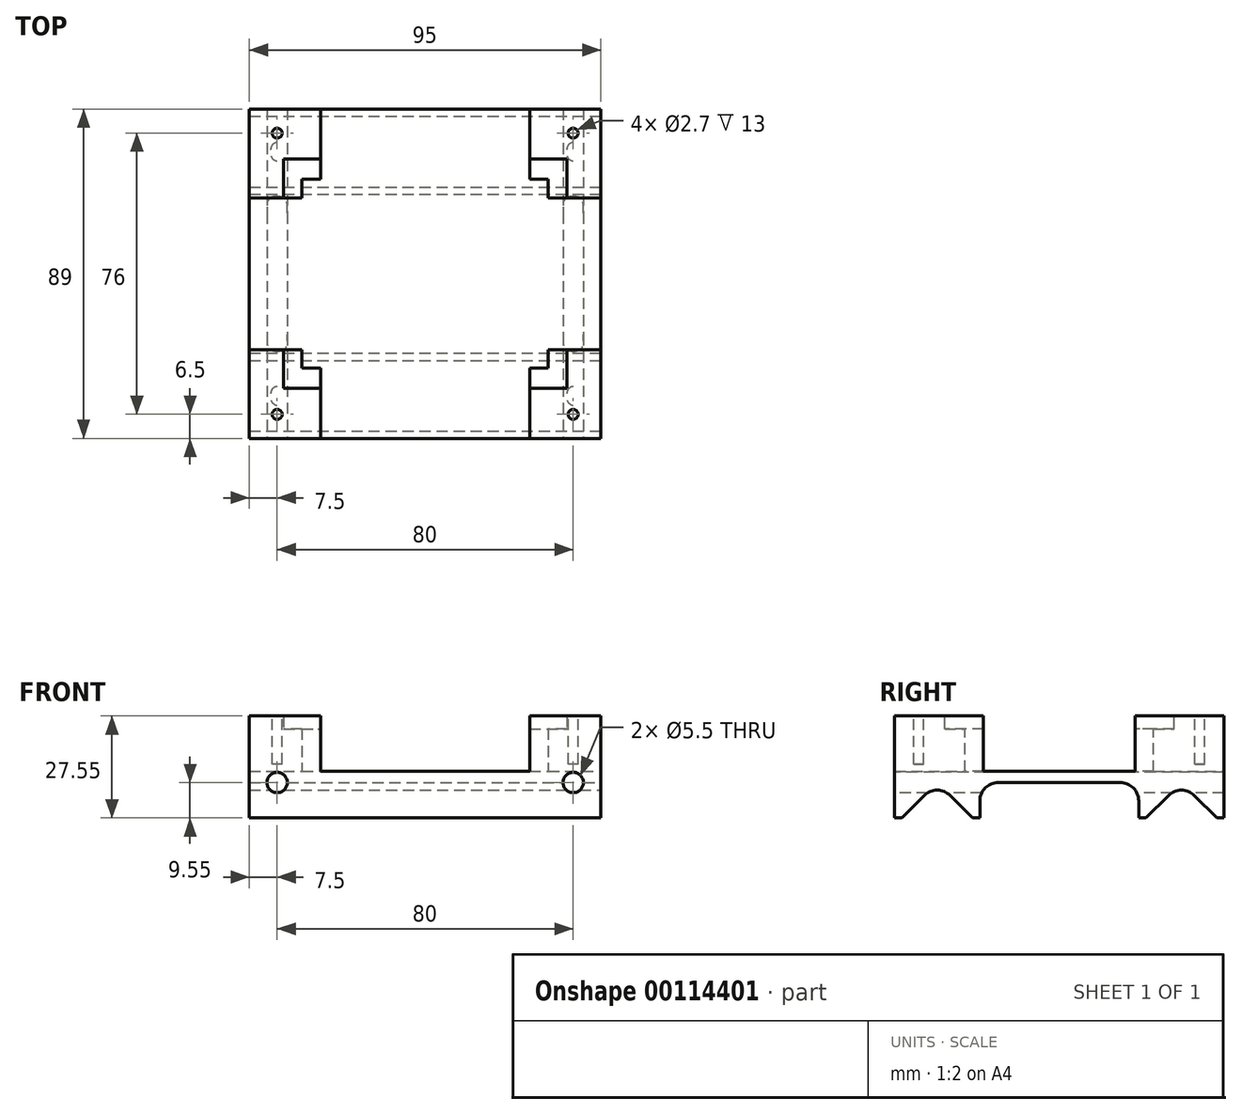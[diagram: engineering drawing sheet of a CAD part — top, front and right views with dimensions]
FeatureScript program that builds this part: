
annotation { "Feature Type Name" : "Feature", "Feature Type Description" : "" }
export const myFeature = defineFeature(function(context is Context, id is Id, definition is map)
    precondition{}
    {
        {
            var Q0;
            Q0=qCreatedBy(makeId("Top.planeOp"),FACE);
            var sketch = newSketch(context, id + "F0", { "sketchPlane" : qUnion([Q0])});
            skLineSegment(sketch, "E0.bottom", {"start": v(0, 0) * mm, "end": v(95, 0) * mm});
            skLineSegment(sketch, "E0.top", {"start": v(0, 89) * mm, "end": v(95, 89) * mm});
            skLineSegment(sketch, "E0.left", {"start": v(0, 0) * mm, "end": v(0, 89) * mm});
            skLineSegment(sketch, "E0.right", {"start": v(95, 0) * mm, "end": v(95, 89) * mm});
            skSolve(sketch);
        }
        {
            var Q0;
            Q0=makeQuery(id+"F0.imprint","IMPRINT",FACE,{"disambiguationData":[TD([[makeQuery(id+"F0.imprint","IMPRINT",EDGE,{"derivedFrom":sQuery(id+"F0.wireOp",EDGE,"E0.bottom")}),1.0]])]});
            extrude(context, id + "F1", {"entities" : qUnion([Q0]), "depth" : 15 * mm});
        }
        {
            var Q0;
            Q0=makeQuery(id+"F1.opExtrude","CAP_FACE",FACE,{"disambiguationData":[OSD([sQuery(id+"F0.wireOp",EDGE,"E0.bottom"),sQuery(id+"F0.wireOp",EDGE,"E0.top"),sQuery(id+"F0.wireOp",EDGE,"E0.left"),sQuery(id+"F0.wireOp",EDGE,"E0.right")])],"isStart":true});
            var sketch = newSketch(context, id + "F2", { "sketchPlane" : qUnion([Q0])});
            skLineSegment(sketch, "E1.0", {"start": v(0, 0) * mm, "end": v(95, 0) * mm});
            skLineSegment(sketch, "E2.0", {"start": v(0, 0) * mm, "end": v(0, -89) * mm});
            skLineSegment(sketch, "E3.0", {"start": v(0, -89) * mm, "end": v(95, -89) * mm});
            skLineSegment(sketch, "E4.0", {"start": v(95, 0) * mm, "end": v(95, -89) * mm});
            skSolve(sketch);
        }
        {
            var Q0;
            Q0=makeQuery(id+"F2.imprint","IMPRINT",FACE,{"disambiguationData":[TD([[makeQuery(id+"F2.imprint","IMPRINT",EDGE,{"derivedFrom":sQuery(id+"F2.wireOp",EDGE,"E1.0")}),-1.0]])]});
            extrude(context, id + "F3", {"entities" : qUnion([Q0]), "operationType" : NewBodyOperationType.ADD, "depth" : 25 * mm});
        }
        {
            var Q0;
            Q0=makeQuery(id+"F1.opExtrude","CAP_FACE",FACE,{"disambiguationData":[OSD([sQuery(id+"F0.wireOp",EDGE,"E0.bottom"),sQuery(id+"F0.wireOp",EDGE,"E0.top"),sQuery(id+"F0.wireOp",EDGE,"E0.left"),sQuery(id+"F0.wireOp",EDGE,"E0.right")])],"isStart":false});
            var sketch = newSketch(context, id + "F4", { "sketchPlane" : qUnion([Q0])});
            skLineSegment(sketch, "E5", {"start": v(0, 44.5) * mm, "end": v(95, 44.5) * mm, "construction": true});
            skLineSegment(sketch, "E6.bottom", {"start": v(14.25, 70) * mm, "end": v(80.75, 70) * mm});
            skLineSegment(sketch, "E6.top", {"start": v(14.25, 19) * mm, "end": v(80.75, 19) * mm});
            skLineSegment(sketch, "E6.left", {"start": v(14.25, 70) * mm, "end": v(14.25, 19) * mm});
            skLineSegment(sketch, "E6.right", {"start": v(80.75, 70) * mm, "end": v(80.75, 19) * mm});
            skPoint(sketch, "E7", {"position": v(47.5, 70) * mm});
            skPoint(sketch, "E8", {"position": v(14.25, 44.5) * mm});
            skLineSegment(sketch, "E9", {"start": v(47.5, 89) * mm, "end": v(47.5, 0) * mm, "construction": true});
            skSolve(sketch);
        }
        {
            var Q0;
            Q0=makeQuery(id+"F4.imprint","IMPRINT",FACE,{"disambiguationData":[TD([[makeQuery(id+"F4.imprint","IMPRINT",EDGE,{"derivedFrom":sQuery(id+"F4.wireOp",EDGE,"E6.bottom")}),-1.0]])]});
            extrude(context, id + "F5", {"entities" : qUnion([Q0]), "operationType" : NewBodyOperationType.REMOVE, "oppositeDirection" : true, "depth" : 15 * mm});
        }
        {
            var Q0;
            Q0=makeQuery(id+"F1.opExtrude","CAP_FACE",FACE,{"disambiguationData":[OSD([sQuery(id+"F0.wireOp",EDGE,"E0.bottom"),sQuery(id+"F0.wireOp",EDGE,"E0.top"),sQuery(id+"F0.wireOp",EDGE,"E0.left"),sQuery(id+"F0.wireOp",EDGE,"E0.right")])],"isStart":false});
            var sketch = newSketch(context, id + "F6", { "sketchPlane" : qUnion([Q0])});
            skLineSegment(sketch, "E10", {"start": v(0, 44.5) * mm, "end": v(95, 44.5) * mm, "construction": true});
            skLineSegment(sketch, "E11", {"start": v(47.5, 89) * mm, "end": v(47.5, 0) * mm, "construction": true});
            skLineSegment(sketch, "E12.bottom", {"start": v(9.25, 75.5) * mm, "end": v(85.75, 75.5) * mm});
            skLineSegment(sketch, "E12.top", {"start": v(9.25, 13.5) * mm, "end": v(85.75, 13.5) * mm});
            skLineSegment(sketch, "E12.left", {"start": v(9.25, 75.5) * mm, "end": v(9.25, 13.5) * mm});
            skLineSegment(sketch, "E12.right", {"start": v(85.75, 75.5) * mm, "end": v(85.75, 13.5) * mm});
            skPoint(sketch, "E13", {"position": v(9.25, 44.5) * mm});
            skPoint(sketch, "E14", {"position": v(47.5, 75.5) * mm});
            skSolve(sketch);
        }
        {
            var Q0;
            Q0=makeQuery(id+"F6.imprint","IMPRINT",FACE,{"disambiguationData":[TD([[makeQuery(id+"F6.imprint","IMPRINT",EDGE,{"derivedFrom":sQuery(id+"F6.wireOp",EDGE,"E12.bottom")}),-1.0]])]});
            extrude(context, id + "F7", {"entities" : qUnion([Q0]), "operationType" : NewBodyOperationType.REMOVE, "oppositeDirection" : true, "depth" : 3.5 * mm});
        }
        {
            var Q0;
            Q0=makeQuery(id+"F3.boolean.opBoolean","MERGE",FACE,{"derivedFrom":[makeQuery(id+"F1.opExtrude","SWEPT_FACE",FACE,{"disambiguationData":[OSD([sQuery(id+"F0.wireOp",EDGE,"E0.right")])]}),makeQuery(id+"F3.opExtrude","SWEPT_FACE",FACE,{"disambiguationData":[OSD([sQuery(id+"F2.wireOp",EDGE,"E4.0")])]})]});
            var sketch = newSketch(context, id + "F8", { "sketchPlane" : qUnion([Q0])});
            skLineSegment(sketch, "E15", {"start": v(44.5, -25) * mm, "end": v(44.5, 15) * mm, "construction": true});
            skLineSegment(sketch, "E16", {"start": v(11.5, -25) * mm, "end": v(11.5, 0) * mm, "construction": true});
            skCircle(sketch, "E17", {"center": v(11.5, -12.55) * mm, "radius": 6.75 * mm, "construction": true});
            skLineSegment(sketch, "E18", {"start": v(11.5, -3) * mm, "end": v(1.95, -12.55) * mm});
            skLineSegment(sketch, "E19", {"start": v(11.5, -3) * mm, "end": v(21.05, -12.55) * mm});
            skLineSegment(sketch, "E20", {"start": v(0, -3) * mm, "end": v(44.5, -3) * mm, "construction": true});
            skLineSegment(sketch, "E21.bottom", {"start": v(21.05, -12.55) * mm, "end": v(23.05, -12.55) * mm});
            skLineSegment(sketch, "E21.top", {"start": v(21.05, -3) * mm, "end": v(23.05, -3) * mm, "construction": true});
            skLineSegment(sketch, "E21.left", {"start": v(21.05, -12.55) * mm, "end": v(21.05, -3) * mm, "construction": true});
            skLineSegment(sketch, "E21.right", {"start": v(23.05, -12.55) * mm, "end": v(23.05, -3) * mm});
            skLineSegment(sketch, "E22", {"start": v(1.95, -12.55) * mm, "end": v(0, -12.55) * mm, "construction": true});
            skLineSegment(sketch, "E23", {"start": v(1.95, -12.55) * mm, "end": v(4.75, -12.55) * mm, "construction": true});
            skLineSegment(sketch, "E24", {"start": v(4.75, -12.55) * mm, "end": v(11.5, -12.55) * mm, "construction": true});
            skLineSegment(sketch, "E25", {"start": v(18.25, -12.55) * mm, "end": v(11.5, -12.55) * mm, "construction": true});
            skLineSegment(sketch, "E26", {"start": v(23.05, -12.55) * mm, "end": v(44.5, -12.55) * mm, "construction": true});
            skLineSegment(sketch, "E27", {"start": v(18.25, -12.55) * mm, "end": v(21.05, -12.55) * mm, "construction": true});
            skLineSegment(sketch, "E28", {"start": v(23.05, -3) * mm, "end": v(44.5, -3) * mm});
            skLineSegment(sketch, "E29.0", {"start": v(0, 15) * mm, "end": v(0, -25) * mm});
            skLineSegment(sketch, "E30", {"start": v(44.5, -3) * mm, "end": v(44.5, -25) * mm});
            skLineSegment(sketch, "E31.MirrorCS", {"start": v(65.95, -3) * mm, "end": v(44.5, -3) * mm});
            skLineSegment(sketch, "E32.MirrorCS", {"start": v(87.05, -12.55) * mm, "end": v(89, -12.55) * mm, "construction": true});
            skLineSegment(sketch, "E33.MirrorCS", {"start": v(89, 15) * mm, "end": v(89, -25) * mm});
            skLineSegment(sketch, "E34.MirrorCS", {"start": v(65.95, -12.55) * mm, "end": v(44.5, -12.55) * mm, "construction": true});
            skLineSegment(sketch, "E35.MirrorCS", {"start": v(89, -3) * mm, "end": v(44.5, -3) * mm, "construction": true});
            skLineSegment(sketch, "E36.MirrorCS", {"start": v(67.95, -12.55) * mm, "end": v(65.95, -12.55) * mm});
            skLineSegment(sketch, "E37.MirrorCS", {"start": v(77.5, -25) * mm, "end": v(77.5, 0) * mm, "construction": true});
            skLineSegment(sketch, "E38.MirrorCS", {"start": v(70.75, -12.55) * mm, "end": v(67.95, -12.55) * mm, "construction": true});
            skLineSegment(sketch, "E39.MirrorCS", {"start": v(70.75, -12.55) * mm, "end": v(77.5, -12.55) * mm, "construction": true});
            skLineSegment(sketch, "E40.MirrorCS", {"start": v(84.25, -12.55) * mm, "end": v(77.5, -12.55) * mm, "construction": true});
            skCircle(sketch, "E41.MirrorC", {"center": v(77.5, -12.55) * mm, "radius": 6.75 * mm, "construction": true});
            skLineSegment(sketch, "E42.MirrorCS", {"start": v(65.95, -12.55) * mm, "end": v(65.95, -3) * mm});
            skLineSegment(sketch, "E43.MirrorCS", {"start": v(77.5, -3) * mm, "end": v(87.05, -12.55) * mm});
            skLineSegment(sketch, "E44.MirrorCS", {"start": v(67.95, -12.55) * mm, "end": v(67.95, -3) * mm, "construction": true});
            skLineSegment(sketch, "E45.MirrorCS", {"start": v(77.5, -3) * mm, "end": v(67.95, -12.55) * mm});
            skLineSegment(sketch, "E46.MirrorCS", {"start": v(87.05, -12.55) * mm, "end": v(84.25, -12.55) * mm, "construction": true});
            skLineSegment(sketch, "E47.MirrorCS", {"start": v(67.95, -3) * mm, "end": v(65.95, -3) * mm, "construction": true});
            skLineSegment(sketch, "E48", {"start": v(87.05, -12.55) * mm, "end": v(87.05, -3) * mm, "construction": true});
            skLineSegment(sketch, "E49", {"start": v(89.05, -3) * mm, "end": v(89.05, -12.55) * mm});
            skLineSegment(sketch, "E50", {"start": v(87.05, -12.55) * mm, "end": v(89.05, -12.55) * mm});
            skLineSegment(sketch, "E51", {"start": v(89, -3) * mm, "end": v(89.05, -3) * mm});
            skLineSegment(sketch, "E52", {"start": v(-0.05, -3) * mm, "end": v(0, -3) * mm});
            skLineSegment(sketch, "E53", {"start": v(-0.05, -3) * mm, "end": v(-0.05, -12.55) * mm});
            skLineSegment(sketch, "E54", {"start": v(-0.05, -12.55) * mm, "end": v(1.95, -12.55) * mm});
            skLineSegment(sketch, "E55", {"start": v(1.95, -12.55) * mm, "end": v(1.95, -3) * mm, "construction": true});
            skSolve(sketch);
        }
        {
            var Q0;
            Q0=makeQuery(id+"F8.imprint","IMPRINT",FACE,{"disambiguationData":[TD([[makeQuery(id+"F8.imprint","IMPRINT",EDGE,{"derivedFrom":sQuery(id+"F8.wireOp",EDGE,"E18")}),1.0]])]});
            var Q1;
            Q1=makeQuery(id+"F8.imprint","IMPRINT",FACE,{"disambiguationData":[TD([[makeQuery(id+"F8.imprint","IMPRINT",EDGE,{"derivedFrom":sQuery(id+"F8.wireOp",EDGE,"E31.MirrorCS")}),1.0]])]});
            extrude(context, id + "F9", {"entities" : qUnion([Q0, Q1]), "operationType" : NewBodyOperationType.REMOVE, "endBound" : BoundingType.THROUGH_ALL, "oppositeDirection" : true, "depth" : 25 * mm});
        }
        {
            var Q0;
            Q0=makeQuery(id+"F9.boolean.opBoolean","COPY",EDGE,{"derivedFrom":makeQuery(id+"F9.opExtrude","SWEPT_EDGE",EDGE,{"disambiguationData":[OSD([sQuery(id+"F8.wireOp",EDGE,"E18"),sQuery(id+"F8.wireOp",EDGE,"E19")])]})});
            var Q1;
            Q1=makeQuery(id+"F9.boolean.opBoolean","COPY",EDGE,{"derivedFrom":makeQuery(id+"F9.opExtrude","SWEPT_EDGE",EDGE,{"disambiguationData":[OSD([sQuery(id+"F8.wireOp",EDGE,"E43.MirrorCS"),sQuery(id+"F8.wireOp",EDGE,"E45.MirrorCS")])]})});
            fillet(context, id + "F10", {"entities" : qUnion([Q0, Q1]), "radius" : 5 * mm, "tangentPropagation" : true, "allowEdgeOverflow" : false});
        }
        {
            var Q0;
            Q0=makeQuery(id+"F9.boolean.opBoolean","COPY",EDGE,{"derivedFrom":makeQuery(id+"F9.opExtrude","SWEPT_EDGE",EDGE,{"disambiguationData":[OSD([sQuery(id+"F8.wireOp",EDGE,"E31.MirrorCS"),sQuery(id+"F8.wireOp",EDGE,"E42.MirrorCS")])]})});
            var Q1;
            Q1=makeQuery(id+"F9.boolean.opBoolean","COPY",EDGE,{"derivedFrom":makeQuery(id+"F9.opExtrude","SWEPT_EDGE",EDGE,{"disambiguationData":[OSD([sQuery(id+"F8.wireOp",EDGE,"E21.right"),sQuery(id+"F8.wireOp",EDGE,"E28")])]})});
            fillet(context, id + "F11", {"entities" : qUnion([Q0, Q1]), "radius" : 5 * mm, "tangentPropagation" : true, "allowEdgeOverflow" : false});
        }
        {
            var Q0;
            Q0=makeQuery(id+"F3.boolean.opBoolean","MERGE",FACE,{"derivedFrom":[makeQuery(id+"F1.opExtrude","SWEPT_FACE",FACE,{"disambiguationData":[OSD([sQuery(id+"F0.wireOp",EDGE,"E0.bottom")])]}),makeQuery(id+"F3.opExtrude","SWEPT_FACE",FACE,{"disambiguationData":[OSD([sQuery(id+"F2.wireOp",EDGE,"E1.0")])]})]});
            var sketch = newSketch(context, id + "F12", { "sketchPlane" : qUnion([Q0])});
            skLineSegment(sketch, "E56.0", {"start": v(14.25, 0) * mm, "end": v(80.75, 0) * mm});
            skLineSegment(sketch, "E57", {"start": v(47.5, 15) * mm, "end": v(47.5, -12.55) * mm, "construction": true});
            skLineSegment(sketch, "E58", {"start": v(0, -3) * mm, "end": v(95, -3) * mm, "construction": true});
            skCircle(sketch, "E59", {"center": v(7.5, -3) * mm, "radius": 2.75 * mm});
            skCircle(sketch, "E60.MirrorC", {"center": v(87.5, -3) * mm, "radius": 2.75 * mm});
            skPoint(sketch, "E61", {"position": v(47.5, 15) * mm});
            skSolve(sketch);
        }
        {
            var Q0;
            Q0 = qSketchRegion(id + "F12", true);
            extrude(context, id + "F13", {"entities" : qUnion([Q0]), "operationType" : NewBodyOperationType.REMOVE, "endBound" : BoundingType.THROUGH_ALL, "oppositeDirection" : true, "depth" : 25 * mm});
        }
        {
            var Q0;
            {var subQ0=sQuery(id+"F0.wireOp",EDGE,"E0.left");Q0=makeQuery(id+"FX8cCS0Zmo0nsLz_1.boolean.opBoolean","SPLIT",FACE,{"disambiguationData":[TD([makeQuery(id+"F1.opExtrude","SWEPT_FACE",FACE,{"disambiguationData":[OSD([subQ0])]})])],"derivedFrom":makeQuery(id+"F1.opExtrude","CAP_FACE",FACE,{"disambiguationData":[OSD([sQuery(id+"F0.wireOp",EDGE,"E0.bottom"),sQuery(id+"F0.wireOp",EDGE,"E0.top"),subQ0,sQuery(id+"F0.wireOp",EDGE,"E0.right")])],"isStart":false})});}
            var sketch = newSketch(context, id + "F14", { "sketchPlane" : qUnion([Q0])});
            skLineSegment(sketch, "E62", {"start": v(7.5, 0) * mm, "end": v(7.5, 89) * mm, "construction": true});
            skLineSegment(sketch, "E63.0", {"start": v(9.25, 13.5) * mm, "end": v(85.75, 13.5) * mm});
            skLineSegment(sketch, "E64", {"start": v(47.5, 13.5) * mm, "end": v(47.5, 89) * mm, "construction": true});
            skCircle(sketch, "E65", {"center": v(7.5, 6.5) * mm, "radius": 1.35 * mm});
            skCircle(sketch, "E66", {"center": v(7.5, 82.5) * mm, "radius": 1.35 * mm});
            skCircle(sketch, "E67.MirrorC", {"center": v(87.5, 6.5) * mm, "radius": 1.35 * mm});
            skCircle(sketch, "E68.MirrorC", {"center": v(87.5, 82.5) * mm, "radius": 1.35 * mm});
            skLineSegment(sketch, "E69", {"start": v(0, 44.5) * mm, "end": v(95, 44.5) * mm, "construction": true});
            skSolve(sketch);
        }
        {
            var Q0;
            Q0 = qSketchRegion(id + "F14", true);
            extrude(context, id + "F15", {"entities" : qUnion([Q0]), "operationType" : NewBodyOperationType.REMOVE, "oppositeDirection" : true, "depth" : 13 * mm});
        }
        {
            var Q0;
            Q0=makeQuery(id+"F3.boolean.opBoolean","MERGE",FACE,{"derivedFrom":[makeQuery(id+"F1.opExtrude","SWEPT_FACE",FACE,{"disambiguationData":[OSD([sQuery(id+"F0.wireOp",EDGE,"E0.top")])]}),makeQuery(id+"F3.opExtrude","SWEPT_FACE",FACE,{"disambiguationData":[OSD([sQuery(id+"F2.wireOp",EDGE,"E3.0")])]})]});
            var sketch = newSketch(context, id + "F16", { "sketchPlane" : qUnion([Q0])});
            skLineSegment(sketch, "E70.0.0", {"start": v(-80.75, 0) * mm, "end": v(-14.25, 0) * mm});
            skLineSegment(sketch, "E70.0.2", {"start": v(-14.25, 0) * mm, "end": v(-80.75, 0) * mm, "construction": true});
            skLineSegment(sketch, "E71", {"start": v(-47.5, 15) * mm, "end": v(-47.5, -12.55) * mm, "construction": true});
            skLineSegment(sketch, "E72.bottom", {"start": v(-75.75, 15) * mm, "end": v(-19.25, 15) * mm});
            skLineSegment(sketch, "E72.top", {"start": v(-75.75, 0) * mm, "end": v(-19.25, 0) * mm});
            skLineSegment(sketch, "E72.left", {"start": v(-75.75, 15) * mm, "end": v(-75.75, 0) * mm});
            skLineSegment(sketch, "E72.right", {"start": v(-19.25, 15) * mm, "end": v(-19.25, 0) * mm});
            skLineSegment(sketch, "E73.0.0", {"start": v(-14.25, 0) * mm, "end": v(-14.25, 11.5) * mm});
            skLineSegment(sketch, "E73.0.2", {"start": v(-14.25, 11.5) * mm, "end": v(-14.25, 0) * mm, "construction": true});
            skLineSegment(sketch, "E73.1.1", {"start": v(-80.75, 11.5) * mm, "end": v(-80.75, 0) * mm});
            skLineSegment(sketch, "E73.1.3", {"start": v(-80.75, 0) * mm, "end": v(-80.75, 11.5) * mm, "construction": true});
            skSolve(sketch);
        }
        {
            var Q0;
            Q0=makeQuery(id+"F16.imprint","IMPRINT",FACE,{"disambiguationData":[TD([[makeQuery(id+"F16.imprint","IMPRINT",EDGE,{"derivedFrom":sQuery(id+"F16.wireOp",EDGE,"E72.bottom")}),1.0]])]});
            extrude(context, id + "F17", {"entities" : qUnion([Q0]), "operationType" : NewBodyOperationType.REMOVE, "endBound" : BoundingType.THROUGH_ALL, "oppositeDirection" : true, "depth" : 25 * mm});
        }
        {
            var Q0;
            {var subQ9=sQuery(id+"F8.wireOp",EDGE,"E18");Q0=makeQuery(id+"F8.imprint","IMPRINT",FACE,{"disambiguationData":[TD([[makeQuery(id+"F8.imprint","IMPRINT",EDGE,{"derivedFrom":subQ9}),-1.0]])]});}
            var sketch = newSketch(context, id + "F18", { "sketchPlane" : qUnion([Q0])});
            skLineSegment(sketch, "E74.0", {"start": v(19, 0) * mm, "end": v(19, 11.5) * mm});
            skLineSegment(sketch, "E75.0", {"start": v(70, 0) * mm, "end": v(70, 11.5) * mm});
            skLineSegment(sketch, "E76.bottom", {"start": v(24, 0) * mm, "end": v(65, 0) * mm});
            skLineSegment(sketch, "E76.top", {"start": v(24, 15) * mm, "end": v(65, 15) * mm});
            skLineSegment(sketch, "E76.left", {"start": v(24, 0) * mm, "end": v(24, 15) * mm});
            skLineSegment(sketch, "E76.right", {"start": v(65, 0) * mm, "end": v(65, 15) * mm});
            skLineSegment(sketch, "E77.0.1", {"start": v(70, 0) * mm, "end": v(89, 0) * mm, "construction": true});
            skLineSegment(sketch, "E77.0.3", {"start": v(89, 0) * mm, "end": v(70, 0) * mm, "construction": true});
            skLineSegment(sketch, "E77.0.5", {"start": v(70, 0) * mm, "end": v(19, 0) * mm, "construction": true});
            skLineSegment(sketch, "E77.0.7", {"start": v(19, 0) * mm, "end": v(0, 0) * mm, "construction": true});
            skLineSegment(sketch, "E77.0.9", {"start": v(0, 0) * mm, "end": v(19, 0) * mm, "construction": true});
            skLineSegment(sketch, "E77.0.11", {"start": v(19, 0) * mm, "end": v(70, 0) * mm, "construction": true});
            skLineSegment(sketch, "E77.1.1", {"start": v(13.5, 11.5) * mm, "end": v(19, 11.5) * mm, "construction": true});
            skLineSegment(sketch, "E77.1.3", {"start": v(19, 11.5) * mm, "end": v(70, 11.5) * mm, "construction": true});
            skLineSegment(sketch, "E77.1.5", {"start": v(70, 11.5) * mm, "end": v(75.5, 11.5) * mm, "construction": true});
            skLineSegment(sketch, "E77.1.7", {"start": v(75.5, 11.5) * mm, "end": v(13.5, 11.5) * mm, "construction": true});
            skLineSegment(sketch, "E78.0.1", {"start": v(0, 15) * mm, "end": v(13.5, 15) * mm, "construction": true});
            skLineSegment(sketch, "E78.0.3", {"start": v(13.5, 15) * mm, "end": v(75.5, 15) * mm, "construction": true});
            skLineSegment(sketch, "E78.0.5", {"start": v(75.5, 15) * mm, "end": v(89, 15) * mm, "construction": true});
            skLineSegment(sketch, "E78.0.7", {"start": v(89, 15) * mm, "end": v(0, 15) * mm, "construction": true});
            skSolve(sketch);
        }
        {
            var Q0;
            Q0 = qSketchRegion(id + "F18", true);
            extrude(context, id + "F19", {"entities" : qUnion([Q0]), "operationType" : NewBodyOperationType.REMOVE, "endBound" : BoundingType.THROUGH_ALL, "oppositeDirection" : true, "depth" : 25 * mm});
        }
    });
